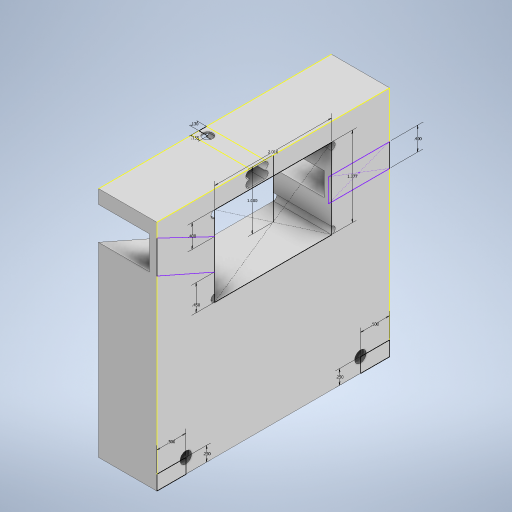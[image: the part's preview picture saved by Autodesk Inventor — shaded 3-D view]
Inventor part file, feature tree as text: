
AUTODESK INVENTOR PART (.ipt)
format: ipt  version: 2024.1 (Build 281209000, 209)  size: 355,840 bytes
history: native  units: in
note: dims shown in document units (in); Inventor stores cm internally (conversion verified against a paired STEP export)
features: sketch x7, extrude x5, hole x3
ambient origin geometry x8: Origin, YZ Plane, XZ Plane, XY Plane, X Axis, Y Axis, Z Axis, Center Point
bodies: Solid1 (feature_tree)
feature tree (15):
  extrude  "Extrusion1"  Depth=4.0in
  sketch  "Sketch2"  dims[d2=1.0in d3=0.0in d4=0.5in]
  extrude  "Extrusion2"  Depth=1.0in
  hole  "Hole1"  [1 undecoded]
  extrude  "Extrusion4"  Depth=1.0in
  extrude  "Extrusion5"  Depth=1.377in
  sketch  "Sketch7"  dims[d9=2.01in d10=1.377in]
  hole  "Hole2"  [1 undecoded]
  hole  "Hole3"  [1 undecoded]
  extrude  "Extrusion6"  Depth=1.0in
  sketch  "Sketch1"  dims[d0=4.0in d1=4.0in]
  sketch  "Sketch5"  dims[d5=0.25in d6=0.5in]
  sketch  "Sketch6"  dims[d7=0.25in d8=1.0in]
  sketch  "Sketch8"  dims[d11=1.0in d12=0.0in]
  sketch  "Sketch9"  dims[d13=0.196in d14=1.0in d15=0.375in d16=0.25in d17=0.5635in d18=1.0in d19=0.8108in d20=0.4in d21=0.4in d22=0.45in d28=0.125in d29=0.0in d30=0.277in d31=0.156in d32=0.26in d33=0.26in d34=1.0in d35=0.0in d36=0.13in d37=0.1551in d38=0.17in d39=0.75in d40=0.281in d41=0.138in d42=0.5635in d43=0.25in d44=0.8108in d45=0.104in d46=0.125in d47=0.375in d48=0.25in d49=0.5635in d50=0.432in d51=0.8108in d52=0.0625in d53=0.125in d54=0.0625in d55=0.0625in d56=0.0625in d57=0.0625in d58=0.0625in d59=0.0625in d60=0.0625in d61=0.125in d62=0.125in d63=0.125in d64=0.125in d65=0.125in d66=0.125in d67=0.125in d68=1.0in d69=0.0in]
note: 3 required parameter values undecoded (feature->parameter linkage not recoverable at this tier; creation-order binding heuristic only, values carry confidence <= 0.55)
